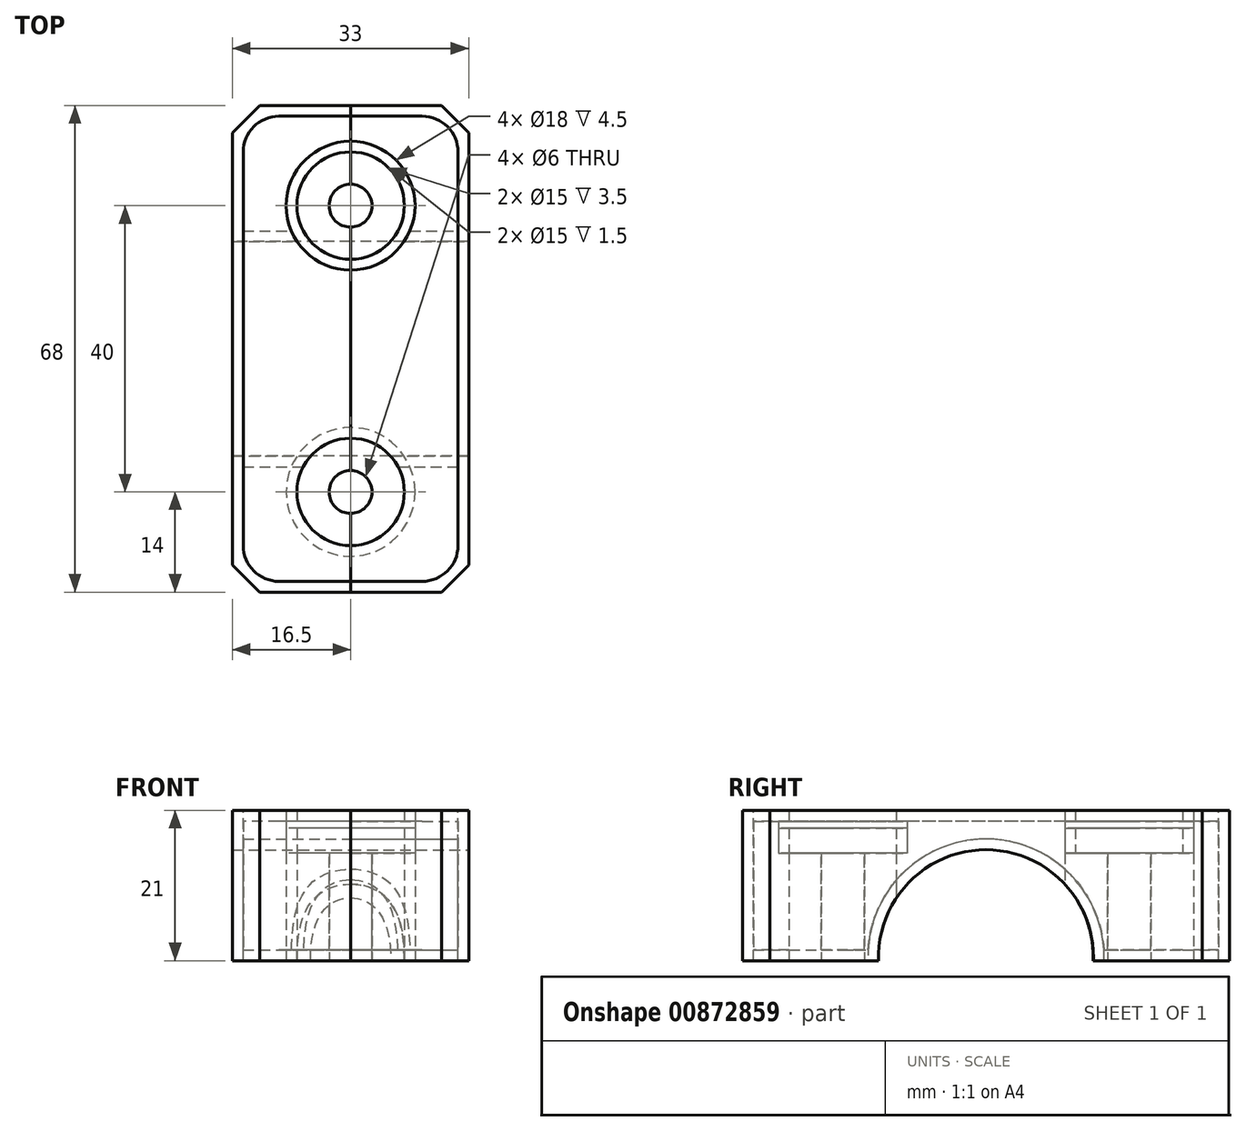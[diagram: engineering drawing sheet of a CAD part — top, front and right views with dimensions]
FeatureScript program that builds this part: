
annotation { "Feature Type Name" : "Feature", "Feature Type Description" : "" }
export const myFeature = defineFeature(function(context is Context, id is Id, definition is map)
    precondition{}
    {
        {
            var Q0;
            Q0=qCreatedBy(makeId("Top.planeOp"),FACE);
            var sketch = newSketch(context, id + "F0", { "sketchPlane" : qUnion([Q0])});
            skLineSegment(sketch, "E0", {"start": v(-10, 32.5) * mm, "end": v(10, 32.5) * mm});
            skLineSegment(sketch, "E1", {"start": v(15, 27.5) * mm, "end": v(15, -27.5) * mm});
            skLineSegment(sketch, "E2", {"start": v(10, -32.5) * mm, "end": v(-10, -32.5) * mm});
            skLineSegment(sketch, "E3", {"start": v(-15, -27.5) * mm, "end": v(-15, 27.5) * mm});
            skLineSegment(sketch, "E4", {"start": v(0, 0) * mm, "end": v(0, 32.5) * mm, "construction": true});
            skLineSegment(sketch, "E5", {"start": v(0, 0) * mm, "end": v(-15, 0) * mm, "construction": true});
            skCircle(sketch, "E6", {"center": v(0, 20) * mm, "radius": 3 * mm});
            skCircle(sketch, "E7", {"center": v(0, -20) * mm, "radius": 3 * mm});
            skLineSegment(sketch, "E8", {"start": v(0, -20) * mm, "end": v(0, 0) * mm, "construction": true});
            skLineSegment(sketch, "E9", {"start": v(0, 0) * mm, "end": v(0, 20) * mm, "construction": true});
            skPoint(sketch, "E10.visualSharp", {"position": v(15, 32.5) * mm});
            skArc(sketch, "E10.filletArc", {"start": v(15, 27.5) * mm, "mid": v(13.54, 31.04) * mm, "end": v(10, 32.5) * mm});
            skPoint(sketch, "E11.visualSharp", {"position": v(15, -32.5) * mm});
            skArc(sketch, "E11.filletArc", {"start": v(10, -32.5) * mm, "mid": v(13.54, -31.04) * mm, "end": v(15, -27.5) * mm});
            skPoint(sketch, "E12.visualSharp", {"position": v(-15, -32.5) * mm});
            skArc(sketch, "E12.filletArc", {"start": v(-15, -27.5) * mm, "mid": v(-13.54, -31.04) * mm, "end": v(-10, -32.5) * mm});
            skPoint(sketch, "E13.visualSharp", {"position": v(-15, 32.5) * mm});
            skArc(sketch, "E13.filletArc", {"start": v(-10, 32.5) * mm, "mid": v(-13.54, 31.04) * mm, "end": v(-15, 27.5) * mm});
            skCircle(sketch, "E14", {"center": v(0, 20) * mm, "radius": 9 * mm});
            skCircle(sketch, "E15", {"center": v(0, -20) * mm, "radius": 9 * mm});
            skLineSegment(sketch, "E16", {"start": v(-12.7, 34) * mm, "end": v(12.7, 34) * mm});
            skLineSegment(sketch, "E17", {"start": v(16.5, 30.2) * mm, "end": v(16.5, -30.2) * mm});
            skLineSegment(sketch, "E18", {"start": v(12.7, -34) * mm, "end": v(-12.7, -34) * mm});
            skLineSegment(sketch, "E19", {"start": v(-16.5, -30.2) * mm, "end": v(-16.5, 30.2) * mm});
            skLineSegment(sketch, "E20", {"start": v(-16.5, 30.2) * mm, "end": v(-12.7, 34) * mm});
            skLineSegment(sketch, "E21.MirrorCS", {"start": v(-46.7, 46.7) * mm, "end": v(-14.2, 46.7) * mm, "construction": true});
            skLineSegment(sketch, "E22", {"start": v(12.7, 34) * mm, "end": v(16.5, 30.2) * mm});
            skLineSegment(sketch, "E23", {"start": v(-16.5, -30.2) * mm, "end": v(-12.7, -34) * mm});
            skLineSegment(sketch, "E24", {"start": v(12.7, -34) * mm, "end": v(16.5, -30.2) * mm});
            skLineSegment(sketch, "E25", {"start": v(0, 34) * mm, "end": v(0, -34) * mm});
            skCircle(sketch, "E26", {"center": v(0, 20) * mm, "radius": 7.5 * mm});
            skCircle(sketch, "E27", {"center": v(0, -20) * mm, "radius": 7.5 * mm});
            skSolve(sketch);
        }
        {
            var Q0;
            Q0=makeQuery(id+"F0.imprint","IMPRINT",FACE,{"disambiguationData":[TD([[makeQuery(id+"F0.imprint","IMPRINT",EDGE,{"derivedFrom":sQuery(id+"F0.wireOp",EDGE,"E0")}),-1.0]])]});
            extrude(context, id + "F1", {"entities" : qUnion([Q0]), "depth" : 4.5 * mm, "offsetDistance" : 25 * mm});
        }
        {
            var Q0;
            Q0=makeQuery(id+"F0.imprint","IMPRINT",FACE,{"disambiguationData":[TD([[makeQuery(id+"F0.imprint","IMPRINT",EDGE,{"derivedFrom":sQuery(id+"F0.wireOp",EDGE,"E6")}),-1.0]])]});
            var Q1;
            Q1=makeQuery(id+"F0.imprint","IMPRINT",FACE,{"disambiguationData":[TD([[makeQuery(id+"F0.imprint","IMPRINT",EDGE,{"derivedFrom":sQuery(id+"F0.wireOp",EDGE,"E7")}),-1.0]])]});
            var Q2;
            Q2=makeQuery(id+"F0.imprint","IMPRINT",FACE,{"disambiguationData":[TD([[makeQuery(id+"F0.imprint","IMPRINT",EDGE,{"derivedFrom":sQuery(id+"F0.wireOp",EDGE,"E0")}),-1.0]])]});
            var Q3;
            {var subQ0=sQuery(id+"F0.wireOp",EDGE,"E25");var subQ1=sQuery(id+"F0.wireOp",EDGE,"E14");var subQ2=makeQuery(id+"F0.imprint","INTERSECT",VERTEX,{"disambiguationData":[OD(0.0)],"derivedFrom":[subQ1,subQ0]});Q3=makeQuery(id+"F0.imprint","IMPRINT",FACE,{"disambiguationData":[TD([[makeQuery(id+"F0.imprint","IMPRINT",EDGE,{"disambiguationData":[TD([[subQ2,-1.0]])],"derivedFrom":subQ1}),1.0]])]});}
            var Q4;
            {var subQ0=sQuery(id+"F0.wireOp",EDGE,"E25");var subQ1=sQuery(id+"F0.wireOp",EDGE,"E14");var subQ2=makeQuery(id+"F0.imprint","INTERSECT",VERTEX,{"disambiguationData":[OD(0.0)],"derivedFrom":[subQ1,subQ0]});Q4=makeQuery(id+"F0.imprint","IMPRINT",FACE,{"disambiguationData":[TD([[makeQuery(id+"F0.imprint","IMPRINT",EDGE,{"disambiguationData":[TD([[subQ2,1.0]])],"derivedFrom":subQ1}),1.0]])]});}
            var Q5;
            {var subQ0=sQuery(id+"F0.wireOp",EDGE,"E25");var subQ1=sQuery(id+"F0.wireOp",EDGE,"E15");var subQ2=makeQuery(id+"F0.imprint","INTERSECT",VERTEX,{"disambiguationData":[OD(0.0)],"derivedFrom":[subQ1,subQ0]});Q5=makeQuery(id+"F0.imprint","IMPRINT",FACE,{"disambiguationData":[TD([[makeQuery(id+"F0.imprint","IMPRINT",EDGE,{"disambiguationData":[TD([[subQ2,-1.0]])],"derivedFrom":subQ1}),1.0]])]});}
            var Q6;
            {var subQ0=sQuery(id+"F0.wireOp",EDGE,"E25");var subQ1=sQuery(id+"F0.wireOp",EDGE,"E15");var subQ2=makeQuery(id+"F0.imprint","INTERSECT",VERTEX,{"disambiguationData":[OD(0.0)],"derivedFrom":[subQ1,subQ0]});Q6=makeQuery(id+"F0.imprint","IMPRINT",FACE,{"disambiguationData":[TD([[makeQuery(id+"F0.imprint","IMPRINT",EDGE,{"disambiguationData":[TD([[subQ2,1.0]])],"derivedFrom":subQ1}),1.0]])]});}
            extrude(context, id + "F2", {"entities" : qUnion([Q0, Q1, Q2, Q3, Q4, Q5, Q6]), "operationType" : NewBodyOperationType.ADD, "oppositeDirection" : true, "depth" : 13.5 * mm, "offsetDistance" : 25 * mm});
        }
        {
            var Q0;
            Q0=qCreatedBy(makeId("Right.planeOp"),FACE);
            var sketch = newSketch(context, id + "F3", { "sketchPlane" : qUnion([Q0])});
            skCircle(sketch, "E28", {"center": v(0, -14.5) * mm, "radius": 16.5 * mm});
            skCircle(sketch, "E29", {"center": v(0, -14.5) * mm, "radius": 15 * mm});
            skSolve(sketch);
        }
        {
            var Q0;
            Q0=makeQuery(id+"F0.imprint","IMPRINT",FACE,{"disambiguationData":[TD([[makeQuery(id+"F0.imprint","IMPRINT",EDGE,{"derivedFrom":sQuery(id+"F0.wireOp",EDGE,"E0")}),-1.0]])]});
            var Q1;
            Q1=makeQuery(id+"F0.imprint","IMPRINT",FACE,{"disambiguationData":[TD([[makeQuery(id+"F0.imprint","IMPRINT",EDGE,{"derivedFrom":sQuery(id+"F0.wireOp",EDGE,"E7")}),-1.0]])]});
            var Q2;
            Q2=makeQuery(id+"F0.imprint","IMPRINT",FACE,{"disambiguationData":[TD([[makeQuery(id+"F0.imprint","IMPRINT",EDGE,{"derivedFrom":sQuery(id+"F0.wireOp",EDGE,"E6")}),-1.0]])]});
            var Q3;
            {var subQ0=sQuery(id+"F0.wireOp",EDGE,"E25");var subQ1=sQuery(id+"F0.wireOp",EDGE,"E14");var subQ2=makeQuery(id+"F0.imprint","INTERSECT",VERTEX,{"disambiguationData":[OD(0.0)],"derivedFrom":[subQ1,subQ0]});Q3=makeQuery(id+"F0.imprint","IMPRINT",FACE,{"disambiguationData":[TD([[makeQuery(id+"F0.imprint","IMPRINT",EDGE,{"disambiguationData":[TD([[subQ2,-1.0]])],"derivedFrom":subQ1}),1.0]])]});}
            var Q4;
            {var subQ0=sQuery(id+"F0.wireOp",EDGE,"E25");var subQ1=sQuery(id+"F0.wireOp",EDGE,"E14");var subQ2=makeQuery(id+"F0.imprint","INTERSECT",VERTEX,{"disambiguationData":[OD(0.0)],"derivedFrom":[subQ1,subQ0]});Q4=makeQuery(id+"F0.imprint","IMPRINT",FACE,{"disambiguationData":[TD([[makeQuery(id+"F0.imprint","IMPRINT",EDGE,{"disambiguationData":[TD([[subQ2,1.0]])],"derivedFrom":subQ1}),1.0]])]});}
            var Q5;
            {var subQ0=sQuery(id+"F0.wireOp",EDGE,"E25");var subQ1=sQuery(id+"F0.wireOp",EDGE,"E15");var subQ2=makeQuery(id+"F0.imprint","INTERSECT",VERTEX,{"disambiguationData":[OD(0.0)],"derivedFrom":[subQ1,subQ0]});Q5=makeQuery(id+"F0.imprint","IMPRINT",FACE,{"disambiguationData":[TD([[makeQuery(id+"F0.imprint","IMPRINT",EDGE,{"disambiguationData":[TD([[subQ2,-1.0]])],"derivedFrom":subQ1}),1.0]])]});}
            var Q6;
            {var subQ0=sQuery(id+"F0.wireOp",EDGE,"E25");var subQ1=sQuery(id+"F0.wireOp",EDGE,"E15");var subQ2=makeQuery(id+"F0.imprint","INTERSECT",VERTEX,{"disambiguationData":[OD(0.0)],"derivedFrom":[subQ1,subQ0]});Q6=makeQuery(id+"F0.imprint","IMPRINT",FACE,{"disambiguationData":[TD([[makeQuery(id+"F0.imprint","IMPRINT",EDGE,{"disambiguationData":[TD([[subQ2,1.0]])],"derivedFrom":subQ1}),1.0]])]});}
            extrude(context, id + "F4", {"entities" : qUnion([Q0, Q1, Q2, Q3, Q4, Q5, Q6]), "oppositeDirection" : true, "depth" : 15 * mm, "offsetDistance" : 25 * mm, "hasSecondDirection" : true, "secondDirectionOppositeDirection" : false, "secondDirectionDepth" : 6 * mm});
        }
        {
            var Q0;
            Q0=makeQuery(id+"F3.imprint","IMPRINT",FACE,{"disambiguationData":[TD([[makeQuery(id+"F3.imprint","IMPRINT",EDGE,{"derivedFrom":sQuery(id+"F3.wireOp",EDGE,"E28")}),1.0]])]});
            extrude(context, id + "F5", {"entities" : qUnion([Q0]), "operationType" : NewBodyOperationType.REMOVE, "oppositeDirection" : true, "depth" : 16 * mm, "offsetDistance" : 25 * mm, "hasSecondDirection" : true, "secondDirectionOppositeDirection" : false, "secondDirectionDepth" : 16 * mm});
        }
        {
            var Q0;
            Q0=makeQuery(id+"F0.imprint","IMPRINT",FACE,{"disambiguationData":[TD([[makeQuery(id+"F0.imprint","IMPRINT",EDGE,{"derivedFrom":sQuery(id+"F0.wireOp",EDGE,"E3")}),1.0]])]});
            var Q1;
            Q1=makeQuery(id+"F0.imprint","IMPRINT",FACE,{"disambiguationData":[TD([[makeQuery(id+"F0.imprint","IMPRINT",EDGE,{"derivedFrom":sQuery(id+"F0.wireOp",EDGE,"E3")}),-1.0]])]});
            var Q2;
            {var subQ0=sQuery(id+"F0.wireOp",EDGE,"E25");var subQ1=sQuery(id+"F0.wireOp",EDGE,"E6");var subQ2=makeQuery(id+"F0.imprint","INTERSECT",VERTEX,{"disambiguationData":[OD(0.0)],"derivedFrom":[subQ1,subQ0]});Q2=makeQuery(id+"F0.imprint","IMPRINT",FACE,{"disambiguationData":[TD([[makeQuery(id+"F0.imprint","IMPRINT",EDGE,{"disambiguationData":[TD([[subQ2,-1.0]])],"derivedFrom":subQ1}),-1.0]])]});}
            var Q3;
            {var subQ0=sQuery(id+"F0.wireOp",EDGE,"E25");var subQ1=sQuery(id+"F0.wireOp",EDGE,"E7");var subQ2=makeQuery(id+"F0.imprint","INTERSECT",VERTEX,{"disambiguationData":[OD(0.0)],"derivedFrom":[subQ1,subQ0]});Q3=makeQuery(id+"F0.imprint","IMPRINT",FACE,{"disambiguationData":[TD([[makeQuery(id+"F0.imprint","IMPRINT",EDGE,{"disambiguationData":[TD([[subQ2,-1.0]])],"derivedFrom":subQ1}),-1.0]])]});}
            var Q4;
            {var subQ0=sQuery(id+"F0.wireOp",EDGE,"E25");var subQ1=sQuery(id+"F0.wireOp",EDGE,"E14");var subQ2=makeQuery(id+"F0.imprint","INTERSECT",VERTEX,{"disambiguationData":[OD(0.0)],"derivedFrom":[subQ1,subQ0]});Q4=makeQuery(id+"F0.imprint","IMPRINT",FACE,{"disambiguationData":[TD([[makeQuery(id+"F0.imprint","IMPRINT",EDGE,{"disambiguationData":[TD([[subQ2,-1.0]])],"derivedFrom":subQ1}),1.0]])]});}
            var Q5;
            {var subQ0=sQuery(id+"F0.wireOp",EDGE,"E25");var subQ1=sQuery(id+"F0.wireOp",EDGE,"E15");var subQ2=makeQuery(id+"F0.imprint","INTERSECT",VERTEX,{"disambiguationData":[OD(0.0)],"derivedFrom":[subQ1,subQ0]});Q5=makeQuery(id+"F0.imprint","IMPRINT",FACE,{"disambiguationData":[TD([[makeQuery(id+"F0.imprint","IMPRINT",EDGE,{"disambiguationData":[TD([[subQ2,-1.0]])],"derivedFrom":subQ1}),1.0]])]});}
            extrude(context, id + "F6", {"entities" : qUnion([Q0, Q1, Q2, Q3, Q4, Q5]), "depth" : 6 * mm, "offsetDistance" : 25 * mm, "hasSecondDirection" : true, "secondDirectionOppositeDirection" : true, "secondDirectionDepth" : 15 * mm});
        }
        {
            var Q0;
            Q0=makeQuery(id+"F0.imprint","IMPRINT",FACE,{"disambiguationData":[TD([[makeQuery(id+"F0.imprint","IMPRINT",EDGE,{"derivedFrom":sQuery(id+"F0.wireOp",EDGE,"E1")}),-1.0]])]});
            var Q1;
            Q1=makeQuery(id+"F0.imprint","IMPRINT",FACE,{"disambiguationData":[TD([[makeQuery(id+"F0.imprint","IMPRINT",EDGE,{"derivedFrom":sQuery(id+"F0.wireOp",EDGE,"E1")}),1.0]])]});
            var Q2;
            {var subQ0=sQuery(id+"F0.wireOp",EDGE,"E25");var subQ1=sQuery(id+"F0.wireOp",EDGE,"E14");var subQ2=makeQuery(id+"F0.imprint","INTERSECT",VERTEX,{"disambiguationData":[OD(0.0)],"derivedFrom":[subQ1,subQ0]});Q2=makeQuery(id+"F0.imprint","IMPRINT",FACE,{"disambiguationData":[TD([[makeQuery(id+"F0.imprint","IMPRINT",EDGE,{"disambiguationData":[TD([[subQ2,1.0]])],"derivedFrom":subQ1}),1.0]])]});}
            var Q3;
            {var subQ0=sQuery(id+"F0.wireOp",EDGE,"E25");var subQ1=sQuery(id+"F0.wireOp",EDGE,"E15");var subQ2=makeQuery(id+"F0.imprint","INTERSECT",VERTEX,{"disambiguationData":[OD(0.0)],"derivedFrom":[subQ1,subQ0]});Q3=makeQuery(id+"F0.imprint","IMPRINT",FACE,{"disambiguationData":[TD([[makeQuery(id+"F0.imprint","IMPRINT",EDGE,{"disambiguationData":[TD([[subQ2,1.0]])],"derivedFrom":subQ1}),1.0]])]});}
            var Q4;
            {var subQ0=sQuery(id+"F0.wireOp",EDGE,"E25");var subQ1=sQuery(id+"F0.wireOp",EDGE,"E7");var subQ2=makeQuery(id+"F0.imprint","INTERSECT",VERTEX,{"disambiguationData":[OD(0.0)],"derivedFrom":[subQ1,subQ0]});Q4=makeQuery(id+"F0.imprint","IMPRINT",FACE,{"disambiguationData":[TD([[makeQuery(id+"F0.imprint","IMPRINT",EDGE,{"disambiguationData":[TD([[subQ2,1.0]])],"derivedFrom":subQ1}),-1.0]])]});}
            var Q5;
            {var subQ0=sQuery(id+"F0.wireOp",EDGE,"E25");var subQ1=sQuery(id+"F0.wireOp",EDGE,"E6");var subQ2=makeQuery(id+"F0.imprint","INTERSECT",VERTEX,{"disambiguationData":[OD(0.0)],"derivedFrom":[subQ1,subQ0]});Q5=makeQuery(id+"F0.imprint","IMPRINT",FACE,{"disambiguationData":[TD([[makeQuery(id+"F0.imprint","IMPRINT",EDGE,{"disambiguationData":[TD([[subQ2,1.0]])],"derivedFrom":subQ1}),-1.0]])]});}
            extrude(context, id + "F7", {"entities" : qUnion([Q0, Q1, Q2, Q3, Q4, Q5]), "depth" : 6 * mm, "offsetDistance" : 25 * mm, "hasSecondDirection" : true, "secondDirectionOppositeDirection" : true, "secondDirectionDepth" : 15 * mm});
        }
        {
            var Q0;
            Q0=makeQuery(id+"F1.opExtrude","SWEPT_BODY",BODY,{"disambiguationData":[OSD([sQuery(id+"F0.wireOp",EDGE,"E0"),sQuery(id+"F0.wireOp",EDGE,"E1"),sQuery(id+"F0.wireOp",EDGE,"E2"),sQuery(id+"F0.wireOp",EDGE,"E3"),sQuery(id+"F0.wireOp",EDGE,"E10.filletArc"),sQuery(id+"F0.wireOp",EDGE,"E11.filletArc"),sQuery(id+"F0.wireOp",EDGE,"E12.filletArc"),sQuery(id+"F0.wireOp",EDGE,"E13.filletArc"),sQuery(id+"F0.wireOp",EDGE,"E14"),sQuery(id+"F0.wireOp",EDGE,"E15")])]});
            var Q1;
            Q1=makeQuery(id+"F6.opExtrude","SWEPT_BODY",BODY,{"disambiguationData":[OSD([sQuery(id+"F0.wireOp",EDGE,"E6"),sQuery(id+"F0.wireOp",EDGE,"E7"),sQuery(id+"F0.wireOp",EDGE,"E16"),sQuery(id+"F0.wireOp",EDGE,"E18"),sQuery(id+"F0.wireOp",EDGE,"E19"),sQuery(id+"F0.wireOp",EDGE,"E20"),sQuery(id+"F0.wireOp",EDGE,"E23"),sQuery(id+"F0.wireOp",EDGE,"E25")])]});
            var Q2;
            Q2=makeQuery(id+"F7.opExtrude","SWEPT_BODY",BODY,{"disambiguationData":[OSD([sQuery(id+"F0.wireOp",EDGE,"E6"),sQuery(id+"F0.wireOp",EDGE,"E7"),sQuery(id+"F0.wireOp",EDGE,"E16"),sQuery(id+"F0.wireOp",EDGE,"E17"),sQuery(id+"F0.wireOp",EDGE,"E18"),sQuery(id+"F0.wireOp",EDGE,"E22"),sQuery(id+"F0.wireOp",EDGE,"E24"),sQuery(id+"F0.wireOp",EDGE,"E25")])]});
            booleanBodies(context, id + "F8", {"operationType" : BooleanOperationType.SUBTRACTION, "tools" : qUnion([Q0]), "targets" : qUnion([Q1, Q2]), "keepTools" : true});
        }
        {
            var Q0;
            Q0=makeQuery(id+"F3.imprint","IMPRINT",FACE,{"disambiguationData":[TD([[makeQuery(id+"F3.imprint","IMPRINT",EDGE,{"derivedFrom":sQuery(id+"F3.wireOp",EDGE,"E29")}),1.0]])]});
            extrude(context, id + "F9", {"entities" : qUnion([Q0]), "operationType" : NewBodyOperationType.REMOVE, "depth" : 17 * mm, "offsetDistance" : 25 * mm, "hasSecondDirection" : true, "secondDirectionOppositeDirection" : true, "secondDirectionDepth" : 17 * mm});
        }
        {
            var Q0;
            {var subQ0=sQuery(id+"F0.wireOp",EDGE,"E25");var subQ1=sQuery(id+"F0.wireOp",EDGE,"E7");var subQ2=makeQuery(id+"F0.imprint","INTERSECT",VERTEX,{"disambiguationData":[OD(0.0)],"derivedFrom":[subQ1,subQ0]});Q0=makeQuery(id+"F0.imprint","IMPRINT",FACE,{"disambiguationData":[TD([[makeQuery(id+"F0.imprint","IMPRINT",EDGE,{"disambiguationData":[TD([[subQ2,1.0]])],"derivedFrom":subQ1}),-1.0]])]});}
            var Q1;
            {var subQ0=sQuery(id+"F0.wireOp",EDGE,"E25");var subQ1=sQuery(id+"F0.wireOp",EDGE,"E7");var subQ2=makeQuery(id+"F0.imprint","INTERSECT",VERTEX,{"disambiguationData":[OD(0.0)],"derivedFrom":[subQ1,subQ0]});Q1=makeQuery(id+"F0.imprint","IMPRINT",FACE,{"disambiguationData":[TD([[makeQuery(id+"F0.imprint","IMPRINT",EDGE,{"disambiguationData":[TD([[subQ2,-1.0]])],"derivedFrom":subQ1}),-1.0]])]});}
            var Q2;
            {var subQ0=sQuery(id+"F0.wireOp",EDGE,"E25");var subQ1=sQuery(id+"F0.wireOp",EDGE,"E6");var subQ2=makeQuery(id+"F0.imprint","INTERSECT",VERTEX,{"disambiguationData":[OD(0.0)],"derivedFrom":[subQ1,subQ0]});Q2=makeQuery(id+"F0.imprint","IMPRINT",FACE,{"disambiguationData":[TD([[makeQuery(id+"F0.imprint","IMPRINT",EDGE,{"disambiguationData":[TD([[subQ2,-1.0]])],"derivedFrom":subQ1}),-1.0]])]});}
            var Q3;
            {var subQ0=sQuery(id+"F0.wireOp",EDGE,"E25");var subQ1=sQuery(id+"F0.wireOp",EDGE,"E6");var subQ2=makeQuery(id+"F0.imprint","INTERSECT",VERTEX,{"disambiguationData":[OD(0.0)],"derivedFrom":[subQ1,subQ0]});Q3=makeQuery(id+"F0.imprint","IMPRINT",FACE,{"disambiguationData":[TD([[makeQuery(id+"F0.imprint","IMPRINT",EDGE,{"disambiguationData":[TD([[subQ2,1.0]])],"derivedFrom":subQ1}),-1.0]])]});}
            extrude(context, id + "F10", {"entities" : qUnion([Q0, Q1, Q2, Q3]), "operationType" : NewBodyOperationType.REMOVE, "depth" : 6 * mm, "offsetDistance" : 25 * mm});
        }
        {
            var Q0;
            {var subQ0=sQuery(id+"F0.wireOp",EDGE,"E25");var subQ1=sQuery(id+"F0.wireOp",EDGE,"E15");var subQ2=makeQuery(id+"F0.imprint","INTERSECT",VERTEX,{"disambiguationData":[OD(0.0)],"derivedFrom":[subQ1,subQ0]});Q0=makeQuery(id+"F0.imprint","IMPRINT",FACE,{"disambiguationData":[TD([[makeQuery(id+"F0.imprint","IMPRINT",EDGE,{"disambiguationData":[TD([[subQ2,-1.0]])],"derivedFrom":subQ1}),1.0]])]});}
            var Q1;
            {var subQ0=sQuery(id+"F0.wireOp",EDGE,"E25");var subQ1=sQuery(id+"F0.wireOp",EDGE,"E15");var subQ2=makeQuery(id+"F0.imprint","INTERSECT",VERTEX,{"disambiguationData":[OD(0.0)],"derivedFrom":[subQ1,subQ0]});Q1=makeQuery(id+"F0.imprint","IMPRINT",FACE,{"disambiguationData":[TD([[makeQuery(id+"F0.imprint","IMPRINT",EDGE,{"disambiguationData":[TD([[subQ2,1.0]])],"derivedFrom":subQ1}),1.0]])]});}
            var Q2;
            {var subQ0=sQuery(id+"F0.wireOp",EDGE,"E25");var subQ1=sQuery(id+"F0.wireOp",EDGE,"E14");var subQ2=makeQuery(id+"F0.imprint","INTERSECT",VERTEX,{"disambiguationData":[OD(0.0)],"derivedFrom":[subQ1,subQ0]});Q2=makeQuery(id+"F0.imprint","IMPRINT",FACE,{"disambiguationData":[TD([[makeQuery(id+"F0.imprint","IMPRINT",EDGE,{"disambiguationData":[TD([[subQ2,-1.0]])],"derivedFrom":subQ1}),1.0]])]});}
            var Q3;
            {var subQ0=sQuery(id+"F0.wireOp",EDGE,"E25");var subQ1=sQuery(id+"F0.wireOp",EDGE,"E14");var subQ2=makeQuery(id+"F0.imprint","INTERSECT",VERTEX,{"disambiguationData":[OD(0.0)],"derivedFrom":[subQ1,subQ0]});Q3=makeQuery(id+"F0.imprint","IMPRINT",FACE,{"disambiguationData":[TD([[makeQuery(id+"F0.imprint","IMPRINT",EDGE,{"disambiguationData":[TD([[subQ2,1.0]])],"derivedFrom":subQ1}),1.0]])]});}
            extrude(context, id + "F11", {"entities" : qUnion([Q0, Q1, Q2, Q3]), "operationType" : NewBodyOperationType.REMOVE, "depth" : 4.5 * mm, "offsetDistance" : 25 * mm});
        }
        {
            var Q0;
            {var subQ0=sQuery(id+"F0.wireOp",EDGE,"E25");var subQ1=sQuery(id+"F0.wireOp",EDGE,"E15");var subQ2=makeQuery(id+"F0.imprint","INTERSECT",VERTEX,{"disambiguationData":[OD(0.0)],"derivedFrom":[subQ1,subQ0]});Q0=makeQuery(id+"F0.imprint","IMPRINT",FACE,{"disambiguationData":[TD([[makeQuery(id+"F0.imprint","IMPRINT",EDGE,{"disambiguationData":[TD([[subQ2,1.0]])],"derivedFrom":subQ1}),1.0]])]});}
            var Q1;
            {var subQ0=sQuery(id+"F0.wireOp",EDGE,"E25");var subQ1=sQuery(id+"F0.wireOp",EDGE,"E15");var subQ2=makeQuery(id+"F0.imprint","INTERSECT",VERTEX,{"disambiguationData":[OD(0.0)],"derivedFrom":[subQ1,subQ0]});Q1=makeQuery(id+"F0.imprint","IMPRINT",FACE,{"disambiguationData":[TD([[makeQuery(id+"F0.imprint","IMPRINT",EDGE,{"disambiguationData":[TD([[subQ2,-1.0]])],"derivedFrom":subQ1}),1.0]])]});}
            var Q2;
            {var subQ0=sQuery(id+"F0.wireOp",EDGE,"E25");var subQ1=sQuery(id+"F0.wireOp",EDGE,"E14");var subQ2=makeQuery(id+"F0.imprint","INTERSECT",VERTEX,{"disambiguationData":[OD(0.0)],"derivedFrom":[subQ1,subQ0]});Q2=makeQuery(id+"F0.imprint","IMPRINT",FACE,{"disambiguationData":[TD([[makeQuery(id+"F0.imprint","IMPRINT",EDGE,{"disambiguationData":[TD([[subQ2,-1.0]])],"derivedFrom":subQ1}),1.0]])]});}
            var Q3;
            {var subQ0=sQuery(id+"F0.wireOp",EDGE,"E25");var subQ1=sQuery(id+"F0.wireOp",EDGE,"E14");var subQ2=makeQuery(id+"F0.imprint","INTERSECT",VERTEX,{"disambiguationData":[OD(0.0)],"derivedFrom":[subQ1,subQ0]});Q3=makeQuery(id+"F0.imprint","IMPRINT",FACE,{"disambiguationData":[TD([[makeQuery(id+"F0.imprint","IMPRINT",EDGE,{"disambiguationData":[TD([[subQ2,1.0]])],"derivedFrom":subQ1}),1.0]])]});}
            extrude(context, id + "F12", {"entities" : qUnion([Q0, Q1, Q2, Q3]), "depth" : 3.5 * mm, "offsetDistance" : 25 * mm});
        }
    });
